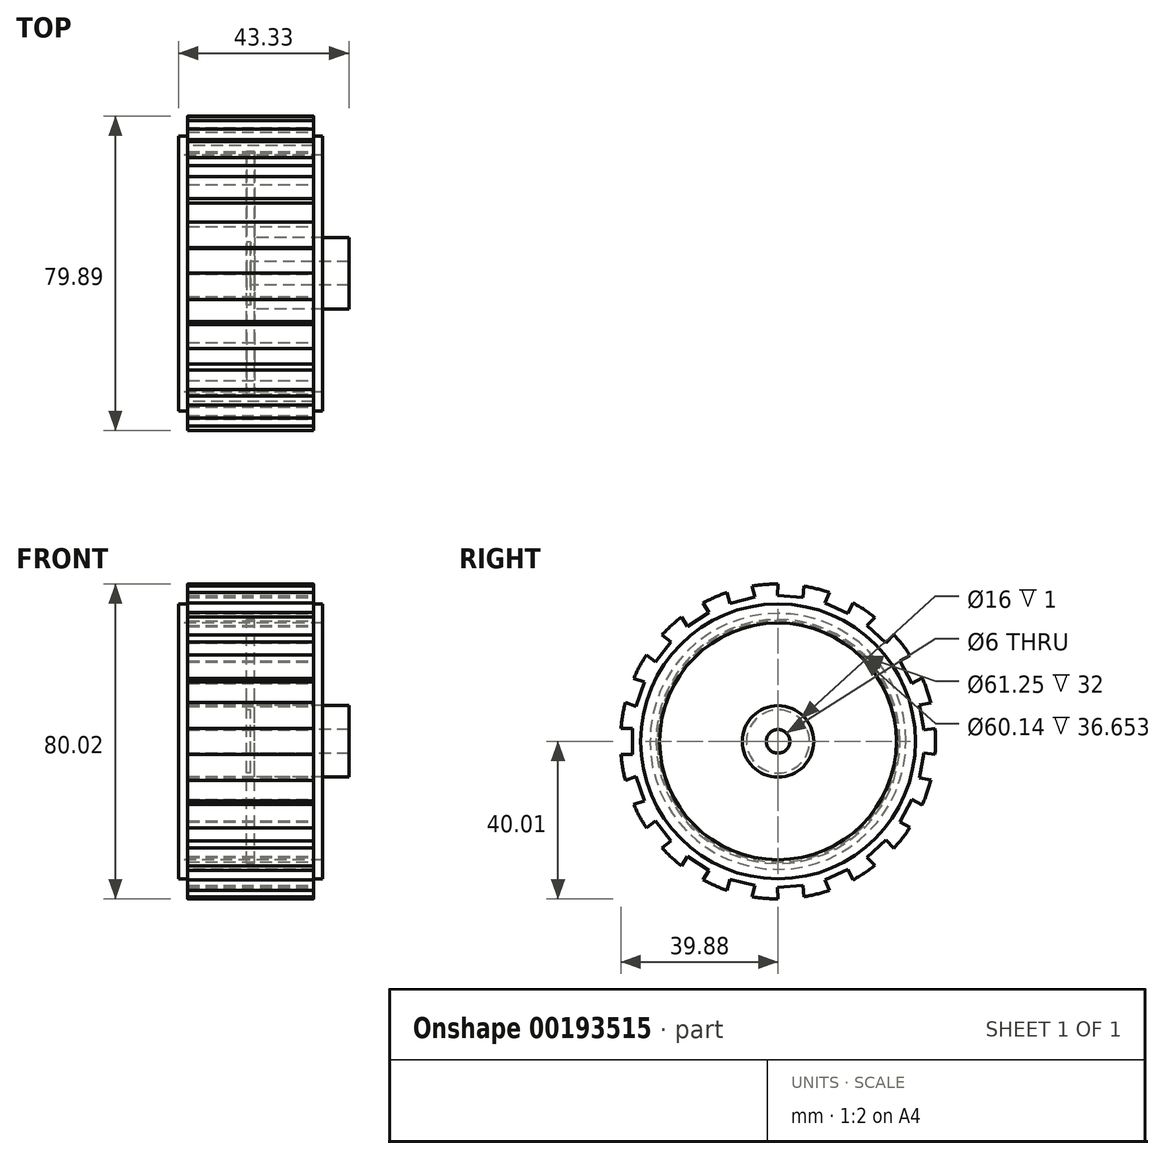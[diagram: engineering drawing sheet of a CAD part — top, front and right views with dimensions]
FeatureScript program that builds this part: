
annotation { "Feature Type Name" : "Feature", "Feature Type Description" : "" }
export const myFeature = defineFeature(function(context is Context, id is Id, definition is map)
    precondition{}
    {
        {
            var Q0;
            Q0=qCreatedBy(makeId("Front.planeOp"),FACE);
            var sketch = newSketch(context, id + "F0", { "sketchPlane" : qUnion([Q0])});
            skLineSegment(sketch, "E0.0", {"start": v(0, 32.5) * mm, "end": v(16, 32.5) * mm});
            skLineSegment(sketch, "E1", {"start": v(16, 32.5) * mm, "end": v(16, 34.92) * mm});
            skLineSegment(sketch, "E2", {"start": v(16, 34.92) * mm, "end": v(18.33, 34.92) * mm});
            skLineSegment(sketch, "E3", {"start": v(18.33, 34.92) * mm, "end": v(18.33, 30.07) * mm});
            skLineSegment(sketch, "E4", {"start": v(18.33, 30.07) * mm, "end": v(0, 30.07) * mm});
            skLineSegment(sketch, "E5.MirrorCS", {"start": v(-16, 32.5) * mm, "end": v(-16, 34.92) * mm});
            skLineSegment(sketch, "E6.MirrorCS", {"start": v(-16, 34.92) * mm, "end": v(-18.33, 34.92) * mm});
            skLineSegment(sketch, "E7.MirrorCS", {"start": v(0, 32.5) * mm, "end": v(-16, 32.5) * mm});
            skLineSegment(sketch, "E8.MirrorCS", {"start": v(-18.33, 34.92) * mm, "end": v(-18.33, 30.07) * mm});
            skLineSegment(sketch, "E9.MirrorCS", {"start": v(-18.33, 30.07) * mm, "end": v(0, 30.07) * mm});
            skLineSegment(sketch, "E10", {"start": v(-8.59, 0) * mm, "end": v(10.8, 0) * mm});
            skSolve(sketch);
        }
        {
            var Q0;
            Q0=makeQuery(id+"F0.imprint","IMPRINT",FACE,{"disambiguationData":[TD([[makeQuery(id+"F0.imprint","IMPRINT",EDGE,{"derivedFrom":sQuery(id+"F0.wireOp",EDGE,"E0.0")}),-1.0]])]});
            var Q1;
            Q1=sQuery(id+"F0.wireOp",EDGE,"E10");
            revolve(context, id + "F1", {"entities" : qUnion([Q0]), "axis" : qUnion([Q1]), "revolveType" : RevolveType.FULL});
        }
        {
            var Q0;
            Q0=qCreatedBy(makeId("Right.planeOp"),FACE);
            var sketch = newSketch(context, id + "F2", { "sketchPlane" : qUnion([Q0])});
            skCircle(sketch, "E11", {"center": v(0, 0) * mm, "radius": 31 * mm});
            skCircle(sketch, "E12", {"center": v(0, 0) * mm, "radius": 8 * mm});
            skCircle(sketch, "E13", {"center": v(0, 0) * mm, "radius": 3 * mm});
            skSolve(sketch);
        }
        {
            var Q0;
            Q0=makeQuery(id+"F2.imprint","IMPRINT",FACE,{"disambiguationData":[TD([[makeQuery(id+"F2.imprint","IMPRINT",EDGE,{"derivedFrom":sQuery(id+"F2.wireOp",EDGE,"E11")}),1.0]])]});
            extrude(context, id + "F3", {"entities" : qUnion([Q0]), "depth" : 1 * mm, "hasSecondDirection" : true, "secondDirectionOppositeDirection" : true, "secondDirectionDepth" : 1 * mm});
        }
        {
            var Q0;
            Q0=qCreatedBy(makeId("Right.planeOp"),FACE);
            var sketch = newSketch(context, id + "F4", { "sketchPlane" : qUnion([Q0])});
            skCircle(sketch, "E14", {"center": v(0, 0) * mm, "radius": 9.08 * mm});
            skCircle(sketch, "E15", {"center": v(0, 0) * mm, "radius": 3 * mm});
            skSolve(sketch);
        }
        {
            var Q0;
            Q0 = qSketchRegion(id + "F4", true);
            extrude(context, id + "F5", {"entities" : qUnion([Q0]), "operationType" : NewBodyOperationType.ADD, "depth" : 25 * mm});
        }
        {
            var Q0;
            Q0=qCreatedBy(makeId("Right.planeOp"),FACE);
            cPlane(context, id + "F6", {"entities" : qUnion([Q0]), "cplaneType" : CPlaneType.OFFSET, "offset" : 16 * mm, "width" : 150 * mm, "height" : 150 * mm});
        }
        {
            var Q0;
            Q0=qCreatedBy(id+"F6.planeOp",FACE);
            var sketch = newSketch(context, id + "F7", { "sketchPlane" : qUnion([Q0])});
            skCircle(sketch, "E16", {"center": v(0, 0) * mm, "radius": 30.63 * mm});
            skCircle(sketch, "E17", {"center": v(0, 0) * mm, "radius": 40.01 * mm});
            skSolve(sketch);
        }
        {
            var Q0;
            Q0 = qSketchRegion(id + "F7", true);
            extrude(context, id + "F8", {"entities" : qUnion([Q0]), "oppositeDirection" : true, "depth" : 32 * mm});
        }
        {
            var Q0;
            Q0=qCreatedBy(id+"F6.planeOp",FACE);
            var sketch = newSketch(context, id + "F9", { "sketchPlane" : qUnion([Q0])});
            skLineSegment(sketch, "E18.bottom", {"start": v(-36.97, -3.26) * mm, "end": v(-46.27, -3.26) * mm});
            skLineSegment(sketch, "E18.top", {"start": v(-36.97, 3.26) * mm, "end": v(-46.27, 3.26) * mm});
            skLineSegment(sketch, "E18.left", {"start": v(-36.97, -3.26) * mm, "end": v(-36.97, 3.26) * mm});
            skLineSegment(sketch, "E18.right", {"start": v(-46.27, -3.26) * mm, "end": v(-46.27, 3.26) * mm});
            skPoint(sketch, "E18.middle", {"position": v(-41.62, 0) * mm});
            skPoint(sketch, "E19.1.0", {"position": v(-39.37, 13.52) * mm});
            skLineSegment(sketch, "E19.1.1", {"start": v(-36.03, 8.93) * mm, "end": v(-44.82, 11.95) * mm});
            skLineSegment(sketch, "E19.1.2", {"start": v(-33.91, 15.08) * mm, "end": v(-42.71, 18.1) * mm});
            skLineSegment(sketch, "E19.1.3", {"start": v(-36.03, 8.93) * mm, "end": v(-33.91, 15.08) * mm});
            skLineSegment(sketch, "E19.1.4", {"start": v(-44.82, 11.95) * mm, "end": v(-42.71, 18.1) * mm});
            skPoint(sketch, "E19.2.0", {"position": v(-32.85, 25.57) * mm});
            skLineSegment(sketch, "E19.2.1", {"start": v(-31.18, 20.14) * mm, "end": v(-38.52, 25.85) * mm});
            skLineSegment(sketch, "E19.2.2", {"start": v(-27.18, 25.28) * mm, "end": v(-34.52, 31) * mm});
            skLineSegment(sketch, "E19.2.3", {"start": v(-31.18, 20.14) * mm, "end": v(-27.18, 25.28) * mm});
            skLineSegment(sketch, "E19.2.4", {"start": v(-38.52, 25.85) * mm, "end": v(-34.52, 31) * mm});
            skPoint(sketch, "E19.3.0", {"position": v(-22.77, 34.85) * mm});
            skLineSegment(sketch, "E19.3.1", {"start": v(-22.95, 29.17) * mm, "end": v(-28.04, 36.96) * mm});
            skLineSegment(sketch, "E19.3.2", {"start": v(-17.5, 32.73) * mm, "end": v(-22.58, 40.52) * mm});
            skLineSegment(sketch, "E19.3.3", {"start": v(-22.95, 29.17) * mm, "end": v(-17.5, 32.73) * mm});
            skLineSegment(sketch, "E19.3.4", {"start": v(-28.04, 36.96) * mm, "end": v(-22.58, 40.52) * mm});
            skPoint(sketch, "E19.4.0", {"position": v(-10.22, 40.35) * mm});
            skLineSegment(sketch, "E19.4.1", {"start": v(-12.23, 35.04) * mm, "end": v(-14.52, 44.06) * mm});
            skLineSegment(sketch, "E19.4.2", {"start": v(-5.92, 36.64) * mm, "end": v(-8.2, 45.66) * mm});
            skLineSegment(sketch, "E19.4.3", {"start": v(-12.23, 35.04) * mm, "end": v(-5.92, 36.64) * mm});
            skLineSegment(sketch, "E19.4.4", {"start": v(-14.52, 44.06) * mm, "end": v(-8.2, 45.66) * mm});
            skPoint(sketch, "E19.5.0", {"position": v(3.44, 41.48) * mm});
            skLineSegment(sketch, "E19.5.1", {"start": v(-0.2, 37.12) * mm, "end": v(0.58, 46.39) * mm});
            skLineSegment(sketch, "E19.5.2", {"start": v(6.3, 36.58) * mm, "end": v(7.07, 45.85) * mm});
            skLineSegment(sketch, "E19.5.3", {"start": v(-0.2, 37.12) * mm, "end": v(6.3, 36.58) * mm});
            skLineSegment(sketch, "E19.5.4", {"start": v(0.58, 46.39) * mm, "end": v(7.07, 45.85) * mm});
            skPoint(sketch, "E19.6.0", {"position": v(16.72, 38.12) * mm});
            skLineSegment(sketch, "E19.6.1", {"start": v(11.87, 35.17) * mm, "end": v(15.6, 43.68) * mm});
            skLineSegment(sketch, "E19.6.2", {"start": v(17.83, 32.55) * mm, "end": v(21.57, 41.07) * mm});
            skLineSegment(sketch, "E19.6.3", {"start": v(11.87, 35.17) * mm, "end": v(17.83, 32.55) * mm});
            skLineSegment(sketch, "E19.6.4", {"start": v(15.6, 43.68) * mm, "end": v(21.57, 41.07) * mm});
            skPoint(sketch, "E19.7.0", {"position": v(28.2, 30.62) * mm});
            skLineSegment(sketch, "E19.7.1", {"start": v(22.65, 29.4) * mm, "end": v(28.95, 36.25) * mm});
            skLineSegment(sketch, "E19.7.2", {"start": v(27.44, 25) * mm, "end": v(33.74, 31.84) * mm});
            skLineSegment(sketch, "E19.7.3", {"start": v(22.65, 29.4) * mm, "end": v(27.44, 25) * mm});
            skLineSegment(sketch, "E19.7.4", {"start": v(28.95, 36.25) * mm, "end": v(33.74, 31.84) * mm});
            skPoint(sketch, "E19.8.0", {"position": v(36.6, 19.81) * mm});
            skLineSegment(sketch, "E19.8.1", {"start": v(30.97, 20.46) * mm, "end": v(39.15, 24.89) * mm});
            skLineSegment(sketch, "E19.8.2", {"start": v(34.07, 14.73) * mm, "end": v(42.25, 19.16) * mm});
            skLineSegment(sketch, "E19.8.3", {"start": v(30.97, 20.46) * mm, "end": v(34.07, 14.73) * mm});
            skLineSegment(sketch, "E19.8.4", {"start": v(39.15, 24.89) * mm, "end": v(42.25, 19.16) * mm});
            skPoint(sketch, "E19.9.0", {"position": v(41.06, 6.85) * mm});
            skLineSegment(sketch, "E19.9.1", {"start": v(35.93, 9.3) * mm, "end": v(45.1, 10.83) * mm});
            skLineSegment(sketch, "E19.9.2", {"start": v(37, 2.87) * mm, "end": v(46.18, 4.4) * mm});
            skLineSegment(sketch, "E19.9.3", {"start": v(35.93, 9.3) * mm, "end": v(37, 2.87) * mm});
            skLineSegment(sketch, "E19.9.4", {"start": v(45.1, 10.83) * mm, "end": v(46.18, 4.4) * mm});
            skPoint(sketch, "E19.10.0", {"position": v(41.06, -6.85) * mm});
            skLineSegment(sketch, "E19.10.1", {"start": v(37, -2.87) * mm, "end": v(46.18, -4.4) * mm});
            skLineSegment(sketch, "E19.10.2", {"start": v(35.93, -9.3) * mm, "end": v(45.1, -10.83) * mm});
            skLineSegment(sketch, "E19.10.3", {"start": v(37, -2.87) * mm, "end": v(35.93, -9.3) * mm});
            skLineSegment(sketch, "E19.10.4", {"start": v(46.18, -4.4) * mm, "end": v(45.1, -10.83) * mm});
            skPoint(sketch, "E19.11.0", {"position": v(36.6, -19.81) * mm});
            skLineSegment(sketch, "E19.11.1", {"start": v(34.07, -14.73) * mm, "end": v(42.25, -19.16) * mm});
            skLineSegment(sketch, "E19.11.2", {"start": v(30.97, -20.46) * mm, "end": v(39.15, -24.89) * mm});
            skLineSegment(sketch, "E19.11.3", {"start": v(34.07, -14.73) * mm, "end": v(30.97, -20.46) * mm});
            skLineSegment(sketch, "E19.11.4", {"start": v(42.25, -19.16) * mm, "end": v(39.15, -24.89) * mm});
            skPoint(sketch, "E19.12.0", {"position": v(28.2, -30.62) * mm});
            skLineSegment(sketch, "E19.12.1", {"start": v(27.44, -25) * mm, "end": v(33.74, -31.84) * mm});
            skLineSegment(sketch, "E19.12.2", {"start": v(22.65, -29.4) * mm, "end": v(28.95, -36.25) * mm});
            skLineSegment(sketch, "E19.12.3", {"start": v(27.44, -25) * mm, "end": v(22.65, -29.4) * mm});
            skLineSegment(sketch, "E19.12.4", {"start": v(33.74, -31.84) * mm, "end": v(28.95, -36.25) * mm});
            skPoint(sketch, "E19.13.0", {"position": v(16.72, -38.12) * mm});
            skLineSegment(sketch, "E19.13.1", {"start": v(17.83, -32.55) * mm, "end": v(21.57, -41.07) * mm});
            skLineSegment(sketch, "E19.13.2", {"start": v(11.87, -35.17) * mm, "end": v(15.6, -43.68) * mm});
            skLineSegment(sketch, "E19.13.3", {"start": v(17.83, -32.55) * mm, "end": v(11.87, -35.17) * mm});
            skLineSegment(sketch, "E19.13.4", {"start": v(21.57, -41.07) * mm, "end": v(15.6, -43.68) * mm});
            skPoint(sketch, "E19.14.0", {"position": v(3.44, -41.48) * mm});
            skLineSegment(sketch, "E19.14.1", {"start": v(6.3, -36.58) * mm, "end": v(7.07, -45.85) * mm});
            skLineSegment(sketch, "E19.14.2", {"start": v(-0.2, -37.12) * mm, "end": v(0.58, -46.39) * mm});
            skLineSegment(sketch, "E19.14.3", {"start": v(6.3, -36.58) * mm, "end": v(-0.2, -37.12) * mm});
            skLineSegment(sketch, "E19.14.4", {"start": v(7.07, -45.85) * mm, "end": v(0.58, -46.39) * mm});
            skPoint(sketch, "E19.15.0", {"position": v(-10.22, -40.35) * mm});
            skLineSegment(sketch, "E19.15.1", {"start": v(-5.92, -36.64) * mm, "end": v(-8.2, -45.66) * mm});
            skLineSegment(sketch, "E19.15.2", {"start": v(-12.23, -35.04) * mm, "end": v(-14.52, -44.06) * mm});
            skLineSegment(sketch, "E19.15.3", {"start": v(-5.92, -36.64) * mm, "end": v(-12.23, -35.04) * mm});
            skLineSegment(sketch, "E19.15.4", {"start": v(-8.2, -45.66) * mm, "end": v(-14.52, -44.06) * mm});
            skPoint(sketch, "E19.16.0", {"position": v(-22.77, -34.85) * mm});
            skLineSegment(sketch, "E19.16.1", {"start": v(-17.5, -32.73) * mm, "end": v(-22.58, -40.52) * mm});
            skLineSegment(sketch, "E19.16.2", {"start": v(-22.95, -29.17) * mm, "end": v(-28.04, -36.96) * mm});
            skLineSegment(sketch, "E19.16.3", {"start": v(-17.5, -32.73) * mm, "end": v(-22.95, -29.17) * mm});
            skLineSegment(sketch, "E19.16.4", {"start": v(-22.58, -40.52) * mm, "end": v(-28.04, -36.96) * mm});
            skPoint(sketch, "E19.17.0", {"position": v(-32.85, -25.57) * mm});
            skLineSegment(sketch, "E19.17.1", {"start": v(-27.18, -25.28) * mm, "end": v(-34.52, -31) * mm});
            skLineSegment(sketch, "E19.17.2", {"start": v(-31.18, -20.14) * mm, "end": v(-38.52, -25.85) * mm});
            skLineSegment(sketch, "E19.17.3", {"start": v(-27.18, -25.28) * mm, "end": v(-31.18, -20.14) * mm});
            skLineSegment(sketch, "E19.17.4", {"start": v(-34.52, -31) * mm, "end": v(-38.52, -25.85) * mm});
            skPoint(sketch, "E19.18.0", {"position": v(-39.37, -13.52) * mm});
            skLineSegment(sketch, "E19.18.1", {"start": v(-33.91, -15.08) * mm, "end": v(-42.71, -18.1) * mm});
            skLineSegment(sketch, "E19.18.2", {"start": v(-36.03, -8.93) * mm, "end": v(-44.82, -11.95) * mm});
            skLineSegment(sketch, "E19.18.3", {"start": v(-33.91, -15.08) * mm, "end": v(-36.03, -8.93) * mm});
            skLineSegment(sketch, "E19.18.4", {"start": v(-42.71, -18.1) * mm, "end": v(-44.82, -11.95) * mm});
            skPoint(sketch, "E19.center", {"position": v(0, 0) * mm});
            skLineSegment(sketch, "E19.anchor1", {"start": v(0, 0) * mm, "end": v(-46.27, -3.26) * mm, "construction": true});
            skLineSegment(sketch, "E19.anchor2", {"start": v(0, 0) * mm, "end": v(-46.27, -3.26) * mm, "construction": true});
            skSolve(sketch);
        }
        {
            var Q0;
            Q0 = qSketchRegion(id + "F9", true);
            extrude(context, id + "F10", {"entities" : qUnion([Q0]), "operationType" : NewBodyOperationType.REMOVE, "oppositeDirection" : true, "depth" : 88 * mm});
        }
    });
